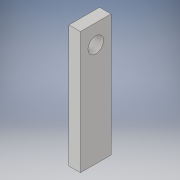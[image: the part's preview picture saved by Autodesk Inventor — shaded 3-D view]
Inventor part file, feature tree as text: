
AUTODESK INVENTOR PART (.ipt)
format: ipt  version: 2019 (Build 230136000, 136)  size: 96,768 bytes
history: native  units: in
note: dims shown in document units (in); Inventor stores cm internally (conversion verified against a paired STEP export)
features: extrude x1, sketch x1
ambient origin geometry x8: Origin, YZ Plane, XZ Plane, XY Plane, X Axis, Y Axis, Z Axis, Center Point
bodies: Solid1 (feature_tree)
feature tree (2):
  extrude  "Extrusion1"  Depth=1.0in
  sketch  "Sketch1"  dims[d0=4.0in d1=1.0in d2=0.51in d3=3.375in d4=0.375in d5=0.0in]
